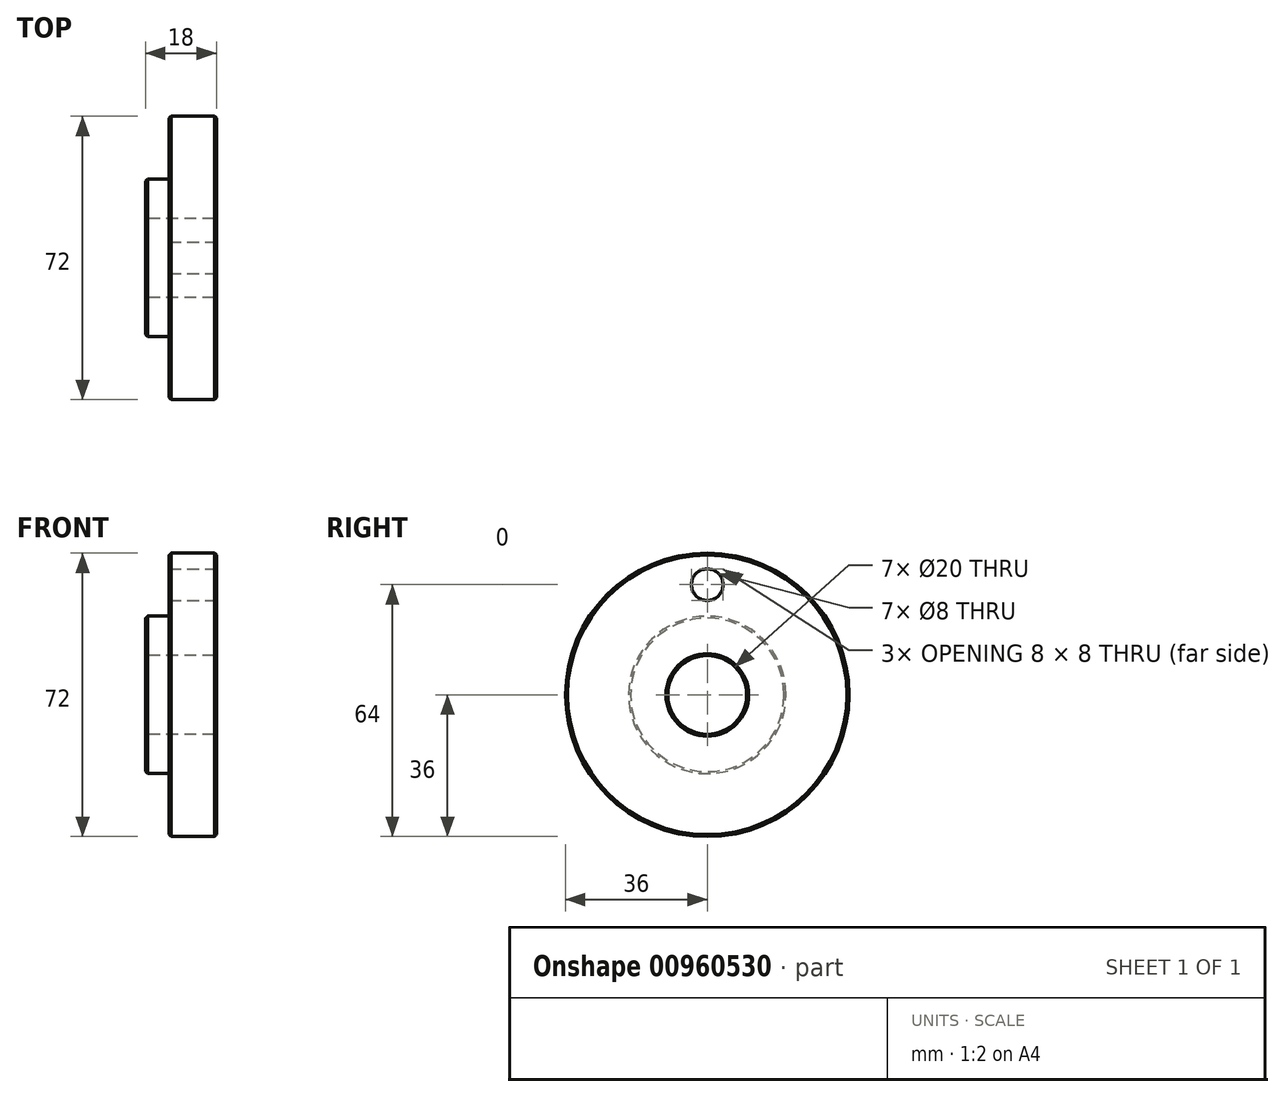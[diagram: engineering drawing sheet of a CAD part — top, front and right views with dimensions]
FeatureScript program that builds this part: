
annotation { "Feature Type Name" : "Feature", "Feature Type Description" : "" }
export const myFeature = defineFeature(function(context is Context, id is Id, definition is map)
    precondition{}
    {
        {
            var Q0;
            Q0=qCreatedBy(makeId("Front.planeOp"),FACE);
            var sketch = newSketch(context, id + "F0", { "sketchPlane" : qUnion([Q0])});
            skLineSegment(sketch, "E0", {"start": v(0, 10) * mm, "end": v(-18, 10) * mm});
            skLineSegment(sketch, "E1", {"start": v(-18, 10) * mm, "end": v(-18, 20) * mm});
            skLineSegment(sketch, "E2", {"start": v(-18, 20) * mm, "end": v(-12, 20) * mm});
            skLineSegment(sketch, "E3", {"start": v(-12, 20) * mm, "end": v(-12, 36) * mm});
            skLineSegment(sketch, "E4", {"start": v(-12, 36) * mm, "end": v(0, 36) * mm});
            skLineSegment(sketch, "E5", {"start": v(0, 36) * mm, "end": v(0, 10) * mm});
            skLineSegment(sketch, "E6", {"start": v(-18, 0) * mm, "end": v(0, 0) * mm, "construction": true});
            skSolve(sketch);
        }
        {
            var Q0;
            Q0=makeQuery(id+"F0.imprint","IMPRINT",FACE,{"disambiguationData":[TD([[makeQuery(id+"F0.imprint","IMPRINT",EDGE,{"derivedFrom":sQuery(id+"F0.wireOp",EDGE,"E0")}),-1.0]])]});
            var Q1;
            Q1=sQuery(id+"F0.wireOp",EDGE,"E6");
            revolve(context, id + "F1", {"surfaceOperationType" : NewSurfaceOperationType.NEW, "entities" : qUnion([Q0]), "axis" : qUnion([Q1]), "revolveType" : RevolveType.FULL});
        }
        {
            var Q0;
            Q0=makeQuery(id+"F1.opRevolve","SWEPT_FACE",FACE,{"disambiguationData":[OSD([sQuery(id+"F0.wireOp",EDGE,"E1")])]});
            var Q1;
            Q1=makeQuery(id+"F1.opRevolve","SWEPT_EDGE",EDGE,{"disambiguationData":[OSD([sQuery(id+"F0.wireOp",EDGE,"E3"),sQuery(id+"F0.wireOp",EDGE,"E4")])]});
            var Q2;
            Q2=makeQuery(id+"F1.opRevolve","SWEPT_FACE",FACE,{"disambiguationData":[OSD([sQuery(id+"F0.wireOp",EDGE,"E5")])]});
            chamfer(context, id + "F2", {"entities" : qUnion([Q0, Q1, Q2]), "width" : 0.5 * mm, "tangentPropagation" : true});
        }
        {
            var Q0;
            Q0=qCreatedBy(makeId("Right.planeOp"),FACE);
            var sketch = newSketch(context, id + "F3", { "sketchPlane" : qUnion([Q0])});
            skPoint(sketch, "E7", {"position": v(0, 28) * mm});
            skCircle(sketch, "E8", {"center": v(0, 28) * mm, "radius": 4 * mm});
            skSolve(sketch);
        }
        {
            var Q0;
            Q0 = qSketchRegion(id + "F3", true);
            extrude(context, id + "F4", {"entities" : qUnion([Q0]), "operationType" : NewBodyOperationType.REMOVE, "endBound" : BoundingType.THROUGH_ALL, "oppositeDirection" : true, "depth" : 25 * mm, "offsetDistance" : 25 * mm});
        }
    });
